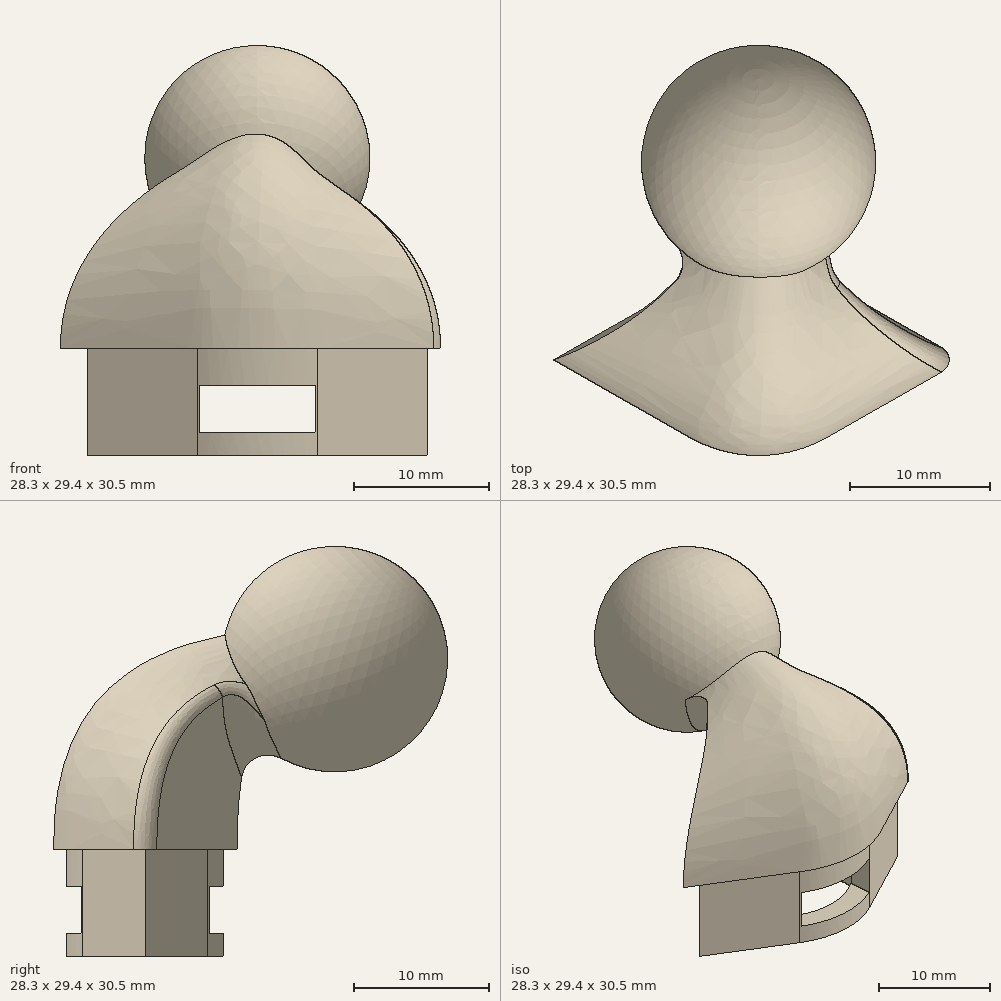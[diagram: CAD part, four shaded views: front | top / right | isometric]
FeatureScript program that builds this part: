
annotation { "Feature Type Name" : "Feature", "Feature Type Description" : "" }
export const myFeature = defineFeature(function(context is Context, id is Id, definition is map)
    precondition{}
    {
        {
            var Q0;
            Q0=qCreatedBy(makeId("Top.planeOp"),FACE);
            var sketch = newSketch(context, id + "F0", { "sketchPlane" : qUnion([Q0])});
            skLineSegment(sketch, "E0", {"start": v(0, 5.85) * mm, "end": v(-12.65, 0) * mm, "construction": true});
            skLineSegment(sketch, "E1", {"start": v(-12.65, 0) * mm, "end": v(0, -5.85) * mm, "construction": true});
            skLineSegment(sketch, "E2", {"start": v(0, -5.85) * mm, "end": v(12.65, 0) * mm, "construction": true});
            skLineSegment(sketch, "E3", {"start": v(12.65, 0) * mm, "end": v(0, 5.85) * mm, "construction": true});
            skLineSegment(sketch, "E4", {"start": v(-12.65, 0) * mm, "end": v(-4.46, 4.67) * mm});
            skLineSegment(sketch, "E5", {"start": v(4.46, 4.67) * mm, "end": v(12.65, 0) * mm});
            skPoint(sketch, "E6.visualSharp", {"position": v(0, 7.2) * mm});
            skArc(sketch, "E6.filletArc", {"start": v(4.46, 4.67) * mm, "mid": v(0, 5.85) * mm, "end": v(-4.46, 4.67) * mm});
            skLineSegment(sketch, "E7", {"start": v(-12.65, 0) * mm, "end": v(-4.46, -4.67) * mm});
            skLineSegment(sketch, "E8", {"start": v(4.46, -4.67) * mm, "end": v(12.65, 0) * mm});
            skPoint(sketch, "E9.visualSharp", {"position": v(0, -7.2) * mm});
            skArc(sketch, "E9.filletArc", {"start": v(-4.46, -4.67) * mm, "mid": v(0, -5.85) * mm, "end": v(4.46, -4.67) * mm});
            skSolve(sketch);
        }
        {
            var Q0;
            Q0 = qSketchRegion(id + "F0", true);
            extrude(context, id + "F1", {"entities" : qUnion([Q0]), "depth" : 8 * mm});
        }
        {
            var Q0;
            Q0=makeQuery(id+"F1.opExtrude","CAP_FACE",FACE,{"disambiguationData":[OSD([sQuery(id+"F0.wireOp",EDGE,"E4"),sQuery(id+"F0.wireOp",EDGE,"E5"),sQuery(id+"F0.wireOp",EDGE,"E6.filletArc"),sQuery(id+"F0.wireOp",EDGE,"E7"),sQuery(id+"F0.wireOp",EDGE,"E8"),sQuery(id+"F0.wireOp",EDGE,"E9.filletArc")])],"isStart":false});
            var sketch = newSketch(context, id + "F2", { "sketchPlane" : qUnion([Q0])});
            skLineSegment(sketch, "E10.0", {"start": v(-14.67, 0) * mm, "end": v(-4.95, -5.54) * mm});
            skLineSegment(sketch, "E10.1", {"start": v(4.95, -5.54) * mm, "end": v(14.67, 0) * mm});
            skLineSegment(sketch, "E10.2", {"start": v(14.67, 0) * mm, "end": v(4.95, 5.54) * mm});
            skArc(sketch, "E10.3", {"start": v(-4.95, -5.54) * mm, "mid": v(0, -6.85) * mm, "end": v(4.95, -5.54) * mm});
            skArc(sketch, "E10.4", {"start": v(4.95, 5.54) * mm, "mid": v(0, 6.85) * mm, "end": v(-4.95, 5.54) * mm});
            skLineSegment(sketch, "E10.5", {"start": v(-4.95, 5.54) * mm, "end": v(-14.67, 0) * mm});
            skSolve(sketch);
        }
        {
            var Q0;
            Q0=qCreatedBy(makeId("Right.planeOp"),FACE);
            var sketch = newSketch(context, id + "F3", { "sketchPlane" : qUnion([Q0])});
            skCircle(sketch, "E11", {"center": v(14.14, 22.14) * mm, "radius": 8.4 * mm});
            skLineSegment(sketch, "E12", {"start": v(0, 8) * mm, "end": v(20.08, 28.08) * mm});
            skSolve(sketch);
        }
        {
            var Q0;
            {var subQ0=sQuery(id+"F3.wireOp",EDGE,"E12");var subQ1=sQuery(id+"F3.wireOp",EDGE,"E11");var subQ2=makeQuery(id+"F3.imprint","INTERSECT",VERTEX,{"disambiguationData":[OD(0.0)],"derivedFrom":[subQ1,subQ0]});Q0=makeQuery(id+"F3.imprint","IMPRINT",FACE,{"disambiguationData":[TD([[makeQuery(id+"F3.imprint","IMPRINT",EDGE,{"disambiguationData":[TD([[subQ2,1.0]])],"derivedFrom":subQ1}),1.0]])]});}
            var Q1;
            Q1=sQuery(id+"F3.wireOp",EDGE,"E12");
            revolve(context, id + "F4", {"entities" : qUnion([Q0]), "axis" : qUnion([Q1]), "revolveType" : RevolveType.FULL});
        }
        {
            var Q0;
            Q0=sQuery(id+"F3.wireOp",VERTEX,"E11.center");
            var Q1;
            Q1=qCreatedBy(makeId("Front.planeOp"),FACE);
            cPlane(context, id + "F5", {"entities" : qUnion([Q0, Q1]), "cplaneType" : CPlaneType.PLANE_POINT, "offset" : 25 * mm, "width" : 150 * mm, "height" : 150 * mm});
        }
        {
            var Q0;
            Q0=qCreatedBy(id+"F5.planeOp",FACE);
            var sketch = newSketch(context, id + "F6", { "sketchPlane" : qUnion([Q0])});
            skCircle(sketch, "E13", {"center": v(0, 22.14) * mm, "radius": 2.5 * mm});
            skSolve(sketch);
        }
        {
            var Q2;
            Q2 = qSketchRegion(id + "F6", true);
            var Q3;
            Q3 = qSketchRegion(id + "F2", true);
            loft(context, id + "F7", {"operationType" : NewBodyOperationType.ADD, "startCondition" : LoftEndDerivativeType.NORMAL_TO_PROFILE, "startMagnitude" : 2, "endCondition" : LoftEndDerivativeType.NORMAL_TO_PROFILE, "endMagnitude" : 2, "sheetProfilesArray" : [{ "sheetProfileEntities" : qUnion([Q2]) }, { "sheetProfileEntities" : qUnion([Q3]) }]});
        }
        {
            var Q0;
            Q0=makeQuery(id+"F7.boolean.opBoolean","INTERSECT",EDGE,{"derivedFrom":[makeQuery(id+"F4.opRevolve","SWEPT_FACE",FACE,{"disambiguationData":[OSD([sQuery(id+"F3.wireOp",EDGE,"E11")])]}),makeQuery(id+"F7.opLoft","SWEPT_FACE",FACE,{"disambiguationData":[OSD([sQuery(id+"F2.wireOp",EDGE,"7323834e-2762-424c-9473-6aa69bbb256c.0"),sQuery(id+"F2.wireOp",EDGE,"7323834e-2762-424c-9473-6aa69bbb256c.1"),sQuery(id+"F2.wireOp",EDGE,"7323834e-2762-424c-9473-6aa69bbb256c.2"),sQuery(id+"F2.wireOp",EDGE,"7323834e-2762-424c-9473-6aa69bbb256c.3"),sQuery(id+"F6.wireOp",EDGE,"E13")])]})]});
            var Q1;
            Q1=makeQuery(id+"F7.boolean.opBoolean","INTERSECT",EDGE,{"derivedFrom":[makeQuery(id+"F4.opRevolve","SWEPT_FACE",FACE,{"disambiguationData":[OSD([sQuery(id+"F3.wireOp",EDGE,"E11")])]}),makeQuery(id+"F7.opLoft","SWEPT_FACE",FACE,{"disambiguationData":[OSD([sQuery(id+"F0.wireOp",EDGE,"E4"),sQuery(id+"F0.wireOp",EDGE,"E7"),sQuery(id+"F2.wireOp",EDGE,"7323834e-2762-424c-9473-6aa69bbb256c.0"),sQuery(id+"F2.wireOp",EDGE,"7323834e-2762-424c-9473-6aa69bbb256c.2"),sQuery(id+"F2.wireOp",EDGE,"7323834e-2762-424c-9473-6aa69bbb256c.4"),sQuery(id+"F2.wireOp",EDGE,"7323834e-2762-424c-9473-6aa69bbb256c.5"),sQuery(id+"F6.wireOp",EDGE,"E13")])]})]});
            fillet(context, id + "F8", {"entities" : qUnion([Q0, Q1]), "radius" : 2 * mm, "tangentPropagation" : true, "allowEdgeOverflow" : false});
        }
        {
            var Q0;
            Q0=makeQuery(id+"F7.opLoft","SWEPT_EDGE",EDGE,{"disambiguationData":[OSD([sQuery(id+"F2.wireOp",EDGE,"7323834e-2762-424c-9473-6aa69bbb256c.1"),sQuery(id+"F2.wireOp",EDGE,"7323834e-2762-424c-9473-6aa69bbb256c.2"),sQuery(id+"F2.wireOp",EDGE,"7323834e-2762-424c-9473-6aa69bbb256c.3"),sQuery(id+"F6.wireOp",EDGE,"E13")])]});
            var Q1;
            Q1=makeQuery(id+"F7.opLoft","SWEPT_EDGE",EDGE,{"disambiguationData":[OSD([sQuery(id+"F2.wireOp",EDGE,"7323834e-2762-424c-9473-6aa69bbb256c.0"),sQuery(id+"F2.wireOp",EDGE,"7323834e-2762-424c-9473-6aa69bbb256c.4"),sQuery(id+"F2.wireOp",EDGE,"7323834e-2762-424c-9473-6aa69bbb256c.5"),sQuery(id+"F6.wireOp",EDGE,"E13")])]});
            fillet(context, id + "F9", {"entities" : qUnion([Q0, Q1]), "radius" : 1 * mm, "tangentPropagation" : true, "allowEdgeOverflow" : false});
        }
        {
            var Q0;
            Q0=makeQuery(id+"F1.opExtrude","CAP_FACE",FACE,{"disambiguationData":[OSD([sQuery(id+"F0.wireOp",EDGE,"E4"),sQuery(id+"F0.wireOp",EDGE,"E5"),sQuery(id+"F0.wireOp",EDGE,"E6.filletArc"),sQuery(id+"F0.wireOp",EDGE,"E7"),sQuery(id+"F0.wireOp",EDGE,"E8"),sQuery(id+"F0.wireOp",EDGE,"E9.filletArc")])],"isStart":true});
            var sketch = newSketch(context, id + "F10", { "sketchPlane" : qUnion([Q0])});
            skLineSegment(sketch, "E14.0", {"start": v(8.61, 0) * mm, "end": v(3.47, 2.93) * mm});
            skLineSegment(sketch, "E14.1", {"start": v(-3.47, 2.93) * mm, "end": v(-8.61, 0) * mm});
            skLineSegment(sketch, "E14.2", {"start": v(-8.61, 0) * mm, "end": v(-3.47, -2.93) * mm});
            skArc(sketch, "E14.3", {"start": v(3.47, 2.93) * mm, "mid": v(0, 3.85) * mm, "end": v(-3.47, 2.93) * mm});
            skArc(sketch, "E14.4", {"start": v(-3.47, -2.93) * mm, "mid": v(0, -3.85) * mm, "end": v(3.47, -2.93) * mm});
            skLineSegment(sketch, "E14.5", {"start": v(3.47, -2.93) * mm, "end": v(8.61, 0) * mm});
            skSolve(sketch);
        }
        {
            var Q0;
            Q0 = qSketchRegion(id + "F10", true);
            extrude(context, id + "F11", {"entities" : qUnion([Q0]), "operationType" : NewBodyOperationType.REMOVE, "oppositeDirection" : true, "depth" : 8 * mm});
        }
        {
            var Q0;
            Q0=qCreatedBy(makeId("Front.planeOp"),FACE);
            var sketch = newSketch(context, id + "F12", { "sketchPlane" : qUnion([Q0])});
            skLineSegment(sketch, "E15.bottom", {"start": v(-4.3, 5.2) * mm, "end": v(4.3, 5.2) * mm});
            skLineSegment(sketch, "E15.top", {"start": v(-4.3, 1.7) * mm, "end": v(4.3, 1.7) * mm});
            skLineSegment(sketch, "E15.left", {"start": v(-4.3, 5.2) * mm, "end": v(-4.3, 1.7) * mm});
            skLineSegment(sketch, "E15.right", {"start": v(4.3, 5.2) * mm, "end": v(4.3, 1.7) * mm});
            skLineSegment(sketch, "E16", {"start": v(0, 1.7) * mm, "end": v(0, 0) * mm, "construction": true});
            skSolve(sketch);
        }
        {
            var Q0;
            Q0 = qSketchRegion(id + "F12", true);
            var Q1;
            Q1=sQuery(id+"F12.wireOp",EDGE,"E16");
            extrude(context, id + "F13", {"entities" : qUnion([Q0]), "operationType" : NewBodyOperationType.REMOVE, "surfaceEntities" : qUnion([Q1]), "oppositeDirection" : true, "depth" : 25 * mm, "hasSecondDirection" : true, "secondDirectionOppositeDirection" : false, "secondDirectionDepth" : 25 * mm});
        }
        {
            var Q0;
            Q0=makeQuery(id+"F11.boolean.opBoolean","COPY",EDGE,{"derivedFrom":makeQuery(id+"F11.opExtrude","SWEPT_EDGE",EDGE,{"disambiguationData":[OSD([sQuery(id+"F10.wireOp",EDGE,"E14.1"),sQuery(id+"F10.wireOp",EDGE,"E14.2")])]})});
            var Q1;
            Q1=makeQuery(id+"F11.boolean.opBoolean","COPY",EDGE,{"derivedFrom":makeQuery(id+"F11.opExtrude","SWEPT_EDGE",EDGE,{"disambiguationData":[OSD([sQuery(id+"F10.wireOp",EDGE,"E14.0"),sQuery(id+"F10.wireOp",EDGE,"E14.5")])]})});
            fillet(context, id + "F14", {"entities" : qUnion([Q0, Q1]), "radius" : 2.5 * mm, "tangentPropagation" : true, "allowEdgeOverflow" : false});
        }
    });
